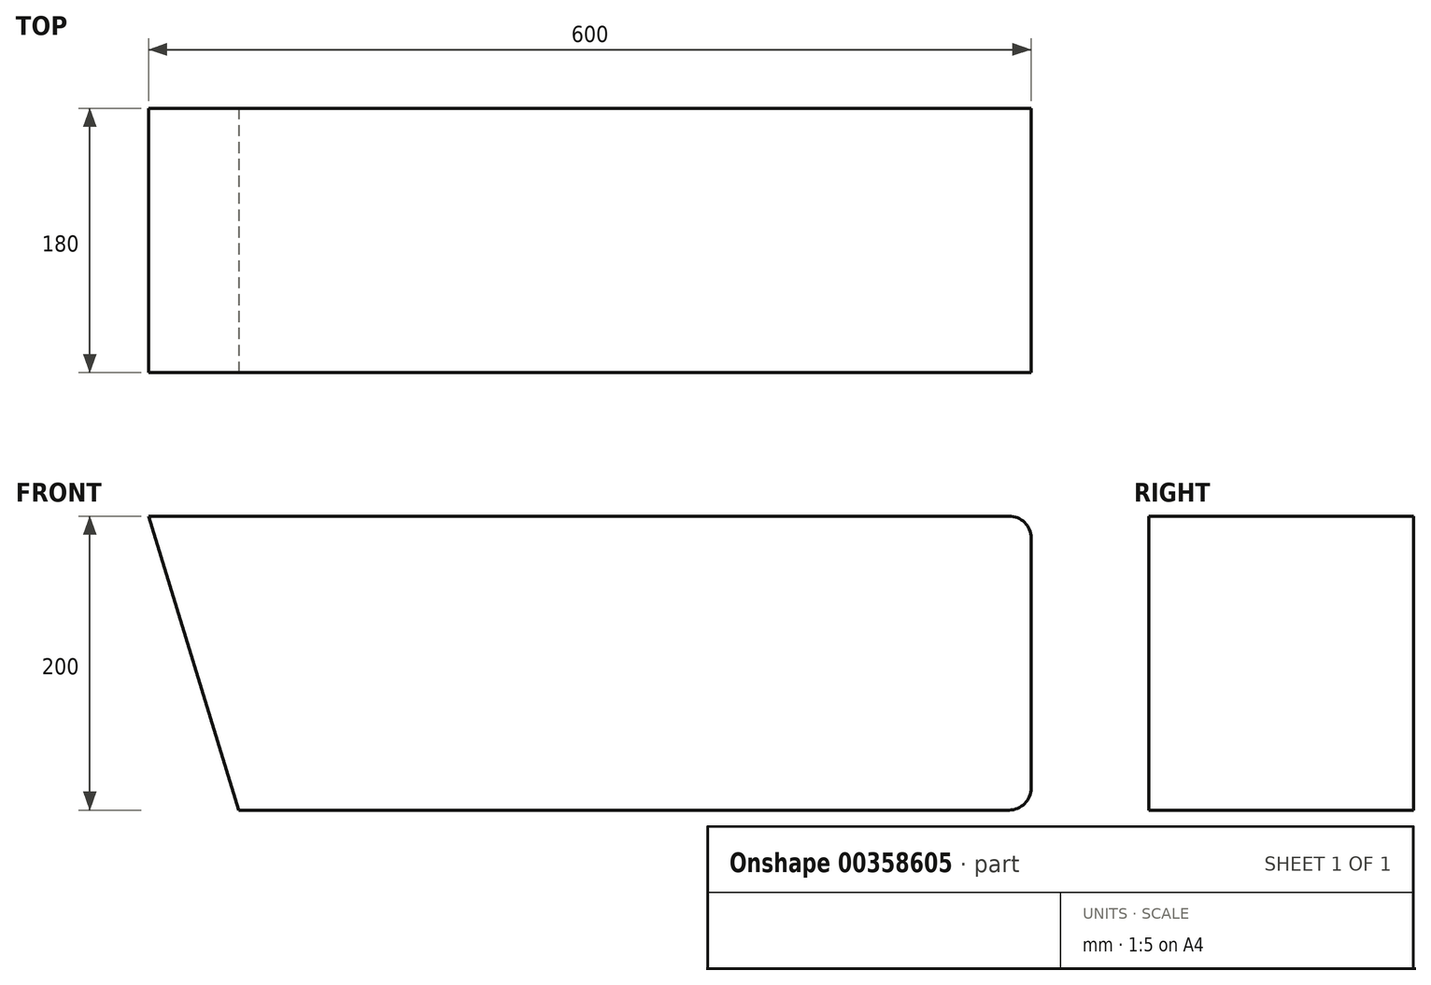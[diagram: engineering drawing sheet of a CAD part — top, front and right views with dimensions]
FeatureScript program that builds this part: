
annotation { "Feature Type Name" : "Feature", "Feature Type Description" : "" }
export const myFeature = defineFeature(function(context is Context, id is Id, definition is map)
    precondition{}
    {
        {
            var Q0;
            Q0=qCreatedBy(makeId("Front.planeOp"),FACE);
            var sketch = newSketch(context, id + "F0", { "sketchPlane" : qUnion([Q0])});
            skLineSegment(sketch, "E0.bottom", {"start": v(300, -100) * mm, "end": v(-300, -100) * mm});
            skLineSegment(sketch, "E0.top", {"start": v(300, 100) * mm, "end": v(-300, 100) * mm});
            skLineSegment(sketch, "E0.left", {"start": v(300, -100) * mm, "end": v(300, 100) * mm});
            skLineSegment(sketch, "E0.right", {"start": v(-300, -100) * mm, "end": v(-300, 100) * mm});
            skPoint(sketch, "E0.middle", {"position": v(0, 0) * mm});
            skSolve(sketch);
        }
        {
            var Q0;
            Q0 = qSketchRegion(id + "F0", true);
            extrude(context, id + "F1", {"entities" : qUnion([Q0]), "oppositeDirection" : true, "depth" : 180 * mm});
        }
        {
            var Q0;
            Q0=makeQuery(id+"F1.opExtrude","CAP_FACE",FACE,{"disambiguationData":[OSD([sQuery(id+"F0.wireOp",EDGE,"E0.bottom"),sQuery(id+"F0.wireOp",EDGE,"E0.top"),sQuery(id+"F0.wireOp",EDGE,"E0.left"),sQuery(id+"F0.wireOp",EDGE,"E0.right")])],"isStart":true});
            var sketch = newSketch(context, id + "F2", { "sketchPlane" : qUnion([Q0])});
            skLineSegment(sketch, "E1", {"start": v(-300, 100) * mm, "end": v(-238.85, -100) * mm});
            skSolve(sketch);
        }
        {
            var Q0;
            {var subQ0=sQuery(id+"F2.wireOp",EDGE,"E1");Q0=makeQuery(id+"F2.imprint","IMPRINT",FACE,{"disambiguationData":[TD([[makeQuery(id+"F2.imprint","IMPRINT",EDGE,{"derivedFrom":subQ0}),-1.0]])]});}
            extrude(context, id + "F3", {"entities" : qUnion([Q0]), "operationType" : NewBodyOperationType.REMOVE, "endBound" : BoundingType.THROUGH_ALL, "oppositeDirection" : true, "depth" : 25 * mm});
        }
        {
            var Q0;
            Q0=makeQuery(id+"F1.opExtrude","SWEPT_EDGE",EDGE,{"disambiguationData":[OSD([sQuery(id+"F0.wireOp",EDGE,"E0.top"),sQuery(id+"F0.wireOp",EDGE,"E0.left")])]});
            var Q1;
            Q1=makeQuery(id+"F1.opExtrude","SWEPT_EDGE",EDGE,{"disambiguationData":[OSD([sQuery(id+"F0.wireOp",EDGE,"E0.bottom"),sQuery(id+"F0.wireOp",EDGE,"E0.left")])]});
            fillet(context, id + "F4", {"entities" : qUnion([Q0, Q1]), "radius" : 15 * mm, "tangentPropagation" : true, "allowEdgeOverflow" : false});
        }
    });
